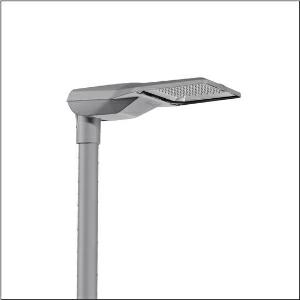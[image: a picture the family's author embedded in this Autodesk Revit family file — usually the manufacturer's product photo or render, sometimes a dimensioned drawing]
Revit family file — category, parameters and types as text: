
# Revit family: streetlight_sl_21_iq_midi___pl52_5xe3h41g08mb_9f92
name_source: partatom
category: Lighting Fixtures
units: mm (PartAtom-declared; Revit-internal decimal feet)

## family parameters
Cut with Voids When Loaded = No
Host = Face
Light Source = No
Part Type = Normal
Room Calculation Point = No
Round Connector Dimension = Use Diameter
Shared = No

## types (1)
- --- (1 x LED, 20000 lm, 146.7 W, 4000K)
    Apparent Load = 147 VA
    CIE Flux Codes = 27 59 98 100 100
    Color Rendering = 70
    Color Temperature = 4000K
    Default Elevation = 1800 mm
    Description = Streetlight SL 21 iQ midi, mast luminaire, primary light control with lens, of PMMA, primary optical cover: cover, of toughened safety glass, transparent, light distribution: PL52, light emission: direct distribution, primary light characteristic: asymmetric, installation type: post-top, side-entry, LED, High Power LED, rated luminous flux: 20.000lm, luminous efficacy: 136lm/W, light colour: 740, colour temperature: 4000K, control: Street-Remote, Auto-Match, Temp-Guard, Lumen-Switch, Night-Set, Smart-Wire, Light-Fading, Desk-Remote (wireless, voltage-free reading and setting of iQ features in the workshop via application-optimized NFC function/RFID function), optimised constant luminous flux control (CLO 2.0), presetting dimming linear, mains connection: 230..240V, AC, 50/60Hz, start of lifetime: 147W, end of service life: 161W, reduction: 62W, luminaire housing, of diecast aluminium, powder-coated, Siteco® metallic grey (DB 702S), corrosivity category C5 mid according to DIN EN ISO 12944, please order mast flange separately, inclination adjustable: 0°, 5°, 10°, 15°, sealing non-destructively replaceable, multi-level sealing system, length: 644mm, width: 335mm, height: 110mm, mast flange for spigot size: 42mm (side-entry): 5XC10008XM4, 60/48mm (side-entry/post-top): 5XC10108XM2, 76/60mm (side-entry/post-top): 5XC10108XM1, protection rating (complete): IP66, insulation class (complete): insulation class II (safety insulation), certification: CE, ENEC, ENEC+, VDE, impact resistance: IK09, permissible operating ambient temperature for outdoor applications: -40..+50°C, standard-compliant lighting for roads and squares, packaging unit: 1 piece

Light Distribution: PL52
    Height = 111 mm
    Lamp = 1 x LED
    Lamp Light Flux = 20000 lm
    Lamp Power = 146.7 W
    Lamp count = 1
    Length = 644 mm
    Luminous efficacy = 136 lm/W
    Manufacturer = Siteco
    ModVariant = No
    Model = 5XE3H41G08MB
    Number of Poles = 1
    OnlyDefault = Yes
    Power Factor = 1
    Product Name = Streetlight SL 21 iQ midi | PL52
    Product group = mast luminaire | pylon top
    ProductGroupID = 6100
    Protection Class = Protection class II
    Protection Degree = IP 66
    RLX_Detail_Level = 1
    RLX_Emergency_Light_Flux = 0 lm
    RLX_Emergency_Type = 0
    RLX_Emergency_Type_DB = No
    RlxData = <blob elided: 100189 chars, md5=8e26acab>
    Socket = socket
    Standby Power = 0 W
    System Light Flux = 20000 lm
    System Power = 147 W
    Type Comments = factory setting: luminous flux: 100 % | dim-lin: 254 | 753 mA
    Type Image = l_1004298.jpg
    URL = http://relux.com
    VarID = @adj_124847
    Voltage = 0 V
    Weight = 0.00 kg
    Width = 336 mm

## geometry (parser evidence)
native form markers: Blend x4, Sweep x11
no freeform markers — native parametric forms only
